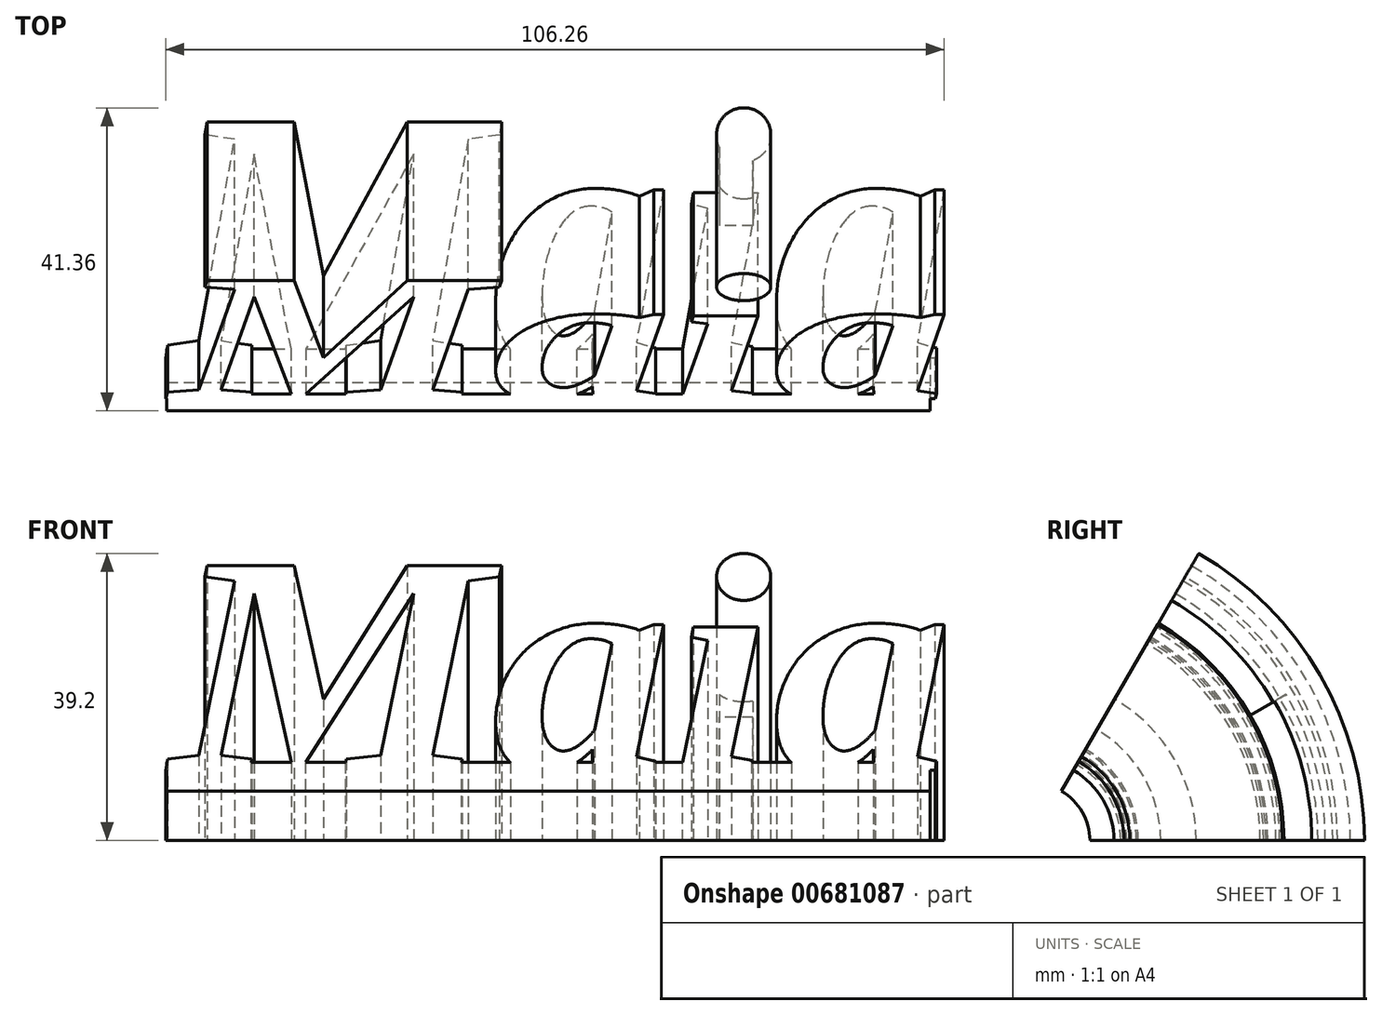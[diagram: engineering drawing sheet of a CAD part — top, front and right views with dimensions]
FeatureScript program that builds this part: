
annotation { "Feature Type Name" : "Feature", "Feature Type Description" : "" }
export const myFeature = defineFeature(function(context is Context, id is Id, definition is map)
    precondition{}
    {
        {
            var Q0;
            Q0=qCreatedBy(makeId("Top.planeOp"),FACE);
            var sketch = newSketch(context, id + "F0", { "sketchPlane" : qUnion([Q0])});
            skText(sketch, "E0", { "text": "Maia", "fontName": "Tinos-BoldItalic.ttf"});
            const initialGuessF0  = {"E0": [-0.07492, -0.01352, 1, 0, 0.03548]};
            skSetInitialGuess(sketch, initialGuessF0);
            skSolve(sketch);
        }
        {
            var Q0;
            Q0=qCreatedBy(makeId("Top.planeOp"),FACE);
            var sketch = newSketch(context, id + "F1", { "sketchPlane" : qUnion([Q0])});
            skLineSegment(sketch, "E1.bottom", {"start": v(-75.42, -12.27) * mm, "end": v(28.75, -12.27) * mm});
            skLineSegment(sketch, "E1.top", {"start": v(-75.42, -16.8) * mm, "end": v(28.75, -16.8) * mm});
            skLineSegment(sketch, "E1.left", {"start": v(-75.42, -12.27) * mm, "end": v(-75.42, -16.8) * mm});
            skLineSegment(sketch, "E1.right", {"start": v(28.75, -12.27) * mm, "end": v(28.75, -16.8) * mm});
            skSolve(sketch);
        }
        {
            var Q0;
            Q0=qCreatedBy(makeId("Top.planeOp"),FACE);
            var sketch = newSketch(context, id + "F2", { "sketchPlane" : qUnion([Q0])});
            skLineSegment(sketch, "E2.bottom", {"start": v(0, 16.67) * mm, "end": v(4.6, 16.67) * mm});
            skLineSegment(sketch, "E2.top", {"start": v(0, 7.36) * mm, "end": v(4.6, 7.36) * mm});
            skLineSegment(sketch, "E2.left", {"start": v(0, 16.67) * mm, "end": v(0, 7.36) * mm});
            skLineSegment(sketch, "E2.right", {"start": v(4.6, 16.67) * mm, "end": v(4.6, 7.36) * mm});
            skSolve(sketch);
        }
        {
            var Q0;
            Q0=qCreatedBy(makeId("Top.planeOp"),FACE);
            var sketch = newSketch(context, id + "F3", { "sketchPlane" : qUnion([Q0])});
            skLineSegment(sketch, "E3", {"start": v(-81.96, -24.6) * mm, "end": v(40.07, -24.6) * mm});
            skSolve(sketch);
        }
        {
            var Q0;
            Q0=makeQuery(id+"F2.imprint","IMPRINT",FACE,{"disambiguationData":[TD([[makeQuery(id+"F2.imprint","IMPRINT",EDGE,{"derivedFrom":sQuery(id+"F2.wireOp",EDGE,"E2.bottom")}),-1.0]])]});
            var Q1;
            Q1=sQuery(id+"F3.wireOp",EDGE,"E3");
            revolve(context, id + "F4", {"entities" : qUnion([Q0]), "axis" : qUnion([Q1]), "revolveType" : RevolveType.ONE_DIRECTION, "angle" : 30 * degree});
        }
        {
            var Q0;
            Q0 = qSketchRegion(id + "F0", true);
            var Q1;
            Q1=makeQuery(id+"F1.imprint","IMPRINT",FACE,{"disambiguationData":[TD([[makeQuery(id+"F1.imprint","IMPRINT",EDGE,{"derivedFrom":sQuery(id+"F1.wireOp",EDGE,"E1.bottom")}),-1.0]])]});
            var Q2;
            Q2=sQuery(id+"F3.wireOp",EDGE,"E3");
            revolve(context, id + "F5", {"operationType" : NewBodyOperationType.ADD, "entities" : qUnion([Q0, Q1]), "axis" : qUnion([Q2]), "revolveType" : RevolveType.ONE_DIRECTION, "angle" : 60 * degree});
        }
    });
